# Revit family: Glazed Face CMU-Top
name_source: partatom
category: Detail Items
revit_build: Autodesk Revit Architecture 2012 (Build: 20110210_1515)
units: mm (PartAtom-declared; Revit-internal decimal feet)

## types (6) — shared parameters
Glazed Thickness = 0' - 0 1/8"
Height = 0' - 7 5/8"
Joint = 0' - 0 3/8"
Length = 1' - 3 5/8"

## per-type parameters (varying)
| type | Core Visibility | Face | Keynote | Thickness | Web |
| 4" x 8" x 16" | Yes | 0' - 0 3/4" | 04 22 00.L2 | 0' - 3 5/8" | 0' - 0 3/4" |
| 2" x 8" x 16" | No | 0' - 0 1/2" | 04 22 00.L1 | 0' - 1 5/8" | 0' - 0 3/4" |
| 6" x 8" x 16" | Yes | 0' - 1" | 04 22 00.L3 | 0' - 5 5/8" | 0' - 1" |
| 10" x 8" x 16" | Yes | 0' - 1 3/8" | 04 22 00.L5 | 0' - 9 5/8" | 0' - 1 1/8" |
| 12" x 8" x 16" | Yes | 0' - 1 1/2" | 04 22 00.L6 | 0' - 11 5/8" | 0' - 1 1/8" |
| 8" x 8" x 16" | Yes | 0' - 1 1/4" | 04 22 00.L4 | 0' - 7 5/8" | 0' - 1" |

## geometry (parser evidence)
native form markers: Sweep x1
no freeform markers — native parametric forms only
